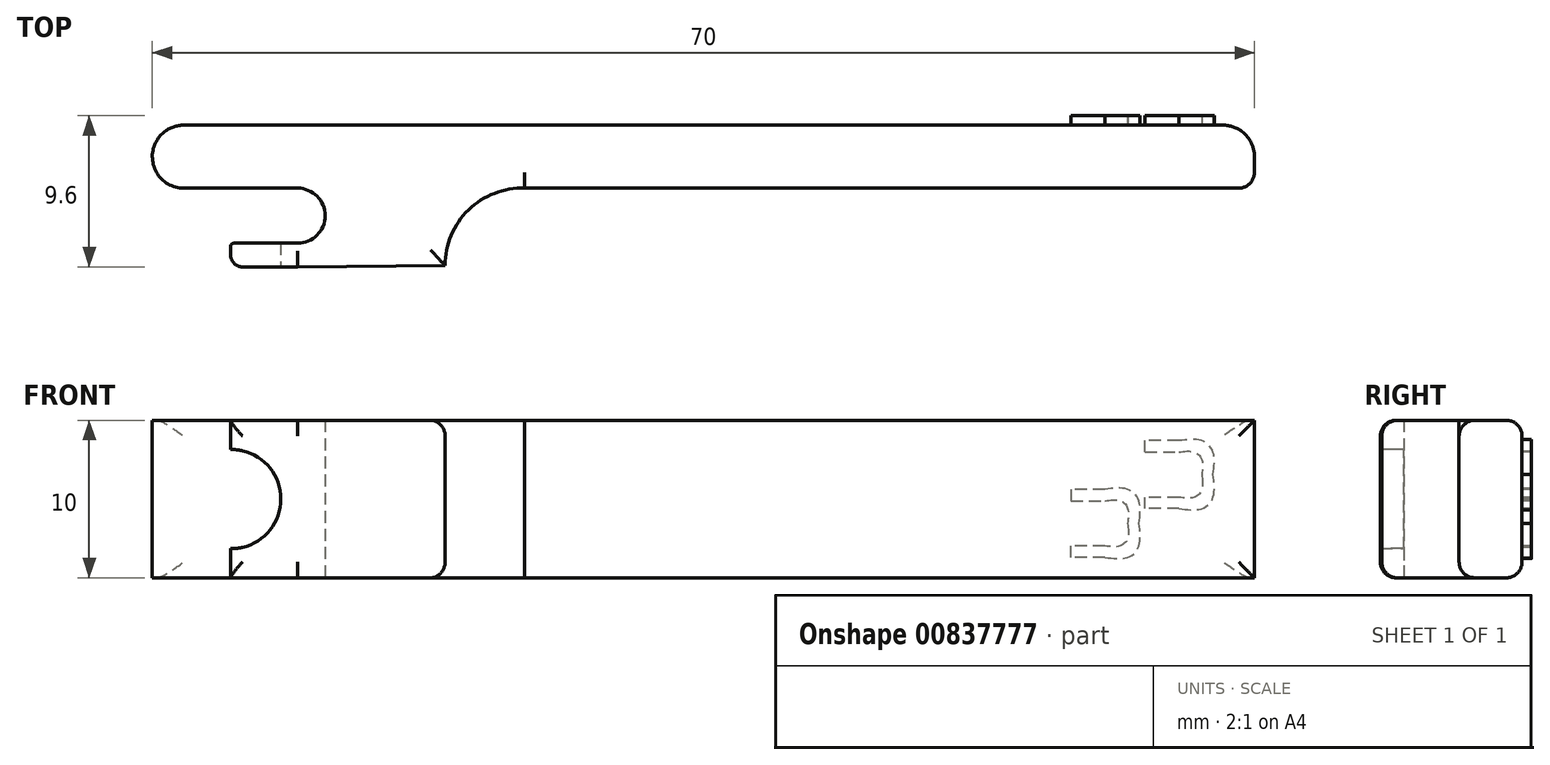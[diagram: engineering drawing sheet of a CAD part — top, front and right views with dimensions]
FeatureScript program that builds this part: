
annotation { "Feature Type Name" : "Feature", "Feature Type Description" : "" }
export const myFeature = defineFeature(function(context is Context, id is Id, definition is map)
    precondition{}
    {
        {
            var Q0;
            Q0=qCreatedBy(makeId("Top.planeOp"),FACE);
            var sketch = newSketch(context, id + "F0", { "sketchPlane" : qUnion([Q0])});
            skLineSegment(sketch, "E0.bottom", {"start": v(-27.18, 4) * mm, "end": v(38.82, 4) * mm});
            skLineSegment(sketch, "E0.top", {"start": v(-27.18, 0) * mm, "end": v(-19.95, 0) * mm});
            skLineSegment(sketch, "E0.left", {"start": v(-29.18, 2) * mm, "end": v(-29.18, 2) * mm});
            skLineSegment(sketch, "E0.right", {"start": v(40.82, 2) * mm, "end": v(40.82, 1) * mm});
            skLineSegment(sketch, "E1.bottom", {"start": v(-5.68, 0) * mm, "end": v(-4.91, 0) * mm});
            skPoint(sketch, "E2.visualSharp", {"position": v(-29.18, 0) * mm});
            skArc(sketch, "E2.filletArc", {"start": v(-29.18, 2) * mm, "mid": v(-28.6, 0.59) * mm, "end": v(-27.18, 0) * mm});
            skPoint(sketch, "E3.visualSharp", {"position": v(-29.18, 4) * mm});
            skArc(sketch, "E3.filletArc", {"start": v(-27.18, 4) * mm, "mid": v(-28.6, 3.41) * mm, "end": v(-29.18, 2) * mm});
            skArc(sketch, "E4", {"start": v(-19.95, -3.5) * mm, "mid": v(-18.2, -1.75) * mm, "end": v(-19.95, 0) * mm});
            skLineSegment(sketch, "E5.right", {"start": v(-4.91, 0) * mm, "end": v(-4.91, 0) * mm});
            skLineSegment(sketch, "E6.bottom", {"start": v(-19.95, -3.5) * mm, "end": v(-24, -3.5) * mm});
            skLineSegment(sketch, "E6.top", {"start": v(-19.95, -5) * mm, "end": v(-23.45, -5) * mm});
            skLineSegment(sketch, "E6.right", {"start": v(-24.2, -3.7) * mm, "end": v(-24.2, -4.25) * mm});
            skPoint(sketch, "E7.visualSharp", {"position": v(-24.2, -5) * mm});
            skArc(sketch, "E7.filletArc", {"start": v(-24.2, -4.25) * mm, "mid": v(-23.98, -4.78) * mm, "end": v(-23.45, -5) * mm});
            skPoint(sketch, "E8.visualSharp", {"position": v(-24.2, -3.5) * mm});
            skArc(sketch, "E8.filletArc", {"start": v(-24, -3.5) * mm, "mid": v(-24.15, -3.56) * mm, "end": v(-24.2, -3.7) * mm});
            skPoint(sketch, "E9.visualSharp", {"position": v(-4.91, -4.9) * mm});
            skPoint(sketch, "E10.visualSharp", {"position": v(40.82, 4) * mm});
            skArc(sketch, "E10.filletArc", {"start": v(40.82, 2) * mm, "mid": v(40.24, 3.41) * mm, "end": v(38.82, 4) * mm});
            skPoint(sketch, "E11.visualSharp", {"position": v(40.82, 0) * mm});
            skArc(sketch, "E11.filletArc", {"start": v(39.82, 0) * mm, "mid": v(40.53, 0.3) * mm, "end": v(40.82, 1) * mm});
            skLineSegment(sketch, "E12.trimOffspring", {"start": v(-4.91, 0) * mm, "end": v(38.32, 0) * mm});
            skLineSegment(sketch, "E13", {"start": v(-18.23, -1.41) * mm, "end": v(-18.2, -5.43) * mm, "construction": true});
            skPoint(sketch, "E13.endSnap0", {"position": v(-18.2, -1.75) * mm});
            skLineSegment(sketch, "E14.top", {"start": v(40.26, 0) * mm, "end": v(39.82, 0) * mm});
            skLineSegment(sketch, "E14.right", {"start": v(38.32, 0) * mm, "end": v(40.26, 0) * mm});
            skPoint(sketch, "E15.end.orphan", {"position": v(-10.58, -4.91) * mm});
            skArc(sketch, "E16", {"start": v(-5.52, 0) * mm, "mid": v(-9.1, -1.38) * mm, "end": v(-10.58, -4.91) * mm});
            skLineSegment(sketch, "E17", {"start": v(-19.95, -5) * mm, "end": v(-10.58, -4.91) * mm});
            skSolve(sketch);
        }
        {
            var Q0;
            Q0=makeQuery(id+"F0.imprint","IMPRINT",FACE,{"disambiguationData":[TD([[makeQuery(id+"F0.imprint","IMPRINT",EDGE,{"derivedFrom":sQuery(id+"F0.wireOp",EDGE,"E0.bottom")}),-1.0]])]});
            extrude(context, id + "F1", {"entities" : qUnion([Q0]), "depth" : 10 * mm, "offsetDistance" : 25 * mm});
        }
        {
            var Q0;
            Q0=makeQuery(id+"F1.opExtrude","CAP_EDGE",EDGE,{"disambiguationData":[OSD([sQuery(id+"F0.wireOp",EDGE,"E12.trimOffspring")])],"isStart":false});
            var Q1;
            Q1=makeQuery(id+"F1.opExtrude","CAP_EDGE",EDGE,{"disambiguationData":[OSD([sQuery(id+"F0.wireOp",EDGE,"E9.filletArc")])],"isStart":false});
            var Q2;
            Q2=makeQuery(id+"F1.opExtrude","CAP_EDGE",EDGE,{"disambiguationData":[OSD([sQuery(id+"F0.wireOp",EDGE,"E9.filletArc")])],"isStart":true});
            var Q3;
            Q3=makeQuery(id+"F1.opExtrude","CAP_EDGE",EDGE,{"disambiguationData":[OSD([sQuery(id+"F0.wireOp",EDGE,"E5.top"),sQuery(id+"F0.wireOp",EDGE,"E6.top")])],"isStart":true});
            var Q4;
            Q4=makeQuery(id+"F1.opExtrude","CAP_EDGE",EDGE,{"disambiguationData":[OSD([sQuery(id+"F0.wireOp",EDGE,"E12.trimOffspring")])],"isStart":true});
            var Q5;
            Q5=makeQuery(id+"F1.opExtrude","CAP_EDGE",EDGE,{"disambiguationData":[OSD([sQuery(id+"F0.wireOp",EDGE,"E0.bottom")])],"isStart":true});
            var Q6;
            Q6=makeQuery(id+"F1.opExtrude","CAP_EDGE",EDGE,{"disambiguationData":[OSD([sQuery(id+"F0.wireOp",EDGE,"E0.bottom")])],"isStart":false});
            var Q7;
            Q7=makeQuery(id+"F1.opExtrude","CAP_EDGE",EDGE,{"disambiguationData":[OSD([sQuery(id+"F0.wireOp",EDGE,"E5.top"),sQuery(id+"F0.wireOp",EDGE,"E6.top")])],"isStart":false});
            var Q8;
            Q8=makeQuery(id+"F1.opExtrude","SWEPT_EDGE",EDGE,{"disambiguationData":[OSD([sQuery(id+"F0.wireOp",EDGE,"E9.filletArc"),sQuery(id+"F0.wireOp",EDGE,"E15")])]});
            var Q9;
            Q9=makeQuery(id+"F1.opExtrude","SWEPT_EDGE",EDGE,{"disambiguationData":[OSD([sQuery(id+"F0.wireOp",EDGE,"E5.top"),sQuery(id+"F0.wireOp",EDGE,"E9.filletArc")])]});
            fillet(context, id + "F2", {"entities" : qUnion([Q0, Q1, Q2, Q3, Q4, Q5, Q6, Q7, Q8, Q9]), "radius" : 1 * mm, "allowEdgeOverflow" : false});
        }
        {
            var Q0;
            Q0=makeQuery(id+"F1.opExtrude","SWEPT_FACE",FACE,{"disambiguationData":[OSD([sQuery(id+"F0.wireOp",EDGE,"E0.bottom")])]});
            var sketch = newSketch(context, id + "F3", { "sketchPlane" : qUnion([Q0])});
            skLineSegment(sketch, "E18", {"start": v(-31.33, 2.02) * mm, "end": v(-29.17, 2.02) * mm});
            skLineSegment(sketch, "E19", {"start": v(-31.33, 5.62) * mm, "end": v(-29.17, 5.62) * mm});
            skLineSegment(sketch, "E20", {"start": v(-29.17, 5.62) * mm, "end": v(-29.17, 4.9) * mm});
            skLineSegment(sketch, "E21", {"start": v(-29.17, 4.9) * mm, "end": v(-31.33, 4.9) * mm});
            skFitSpline(sketch, "E22", {"points": [v(-31.33, 1.3) * mm, v(-32.77, 1.3) * mm, v(-33.49, 2.02) * mm, v(-33.49, 3.46) * mm]});
            skFitSpline(sketch, "E23", {"points": [v(-33.49, 3.46) * mm, v(-33.49, 4.9) * mm, v(-32.77, 5.62) * mm, v(-31.33, 5.62) * mm]});
            skFitSpline(sketch, "E24", {"points": [v(-31.33, 4.9) * mm, v(-32.29, 4.9) * mm, v(-32.77, 4.42) * mm, v(-32.77, 3.46) * mm]});
            skFitSpline(sketch, "E25", {"points": [v(-32.77, 3.46) * mm, v(-32.77, 2.5) * mm, v(-32.29, 2.02) * mm, v(-31.33, 2.02) * mm]});
            skLineSegment(sketch, "E26", {"start": v(-31.33, 1.3) * mm, "end": v(-29.17, 1.3) * mm});
            skLineSegment(sketch, "E27", {"start": v(-29.17, 1.3) * mm, "end": v(-29.17, 2.02) * mm});
            skLineSegment(sketch, "E28", {"start": v(-36.22, 5.11) * mm, "end": v(-33.88, 5.11) * mm});
            skLineSegment(sketch, "E29", {"start": v(-36.04, 8.7) * mm, "end": v(-33.88, 8.7) * mm});
            skLineSegment(sketch, "E30", {"start": v(-33.88, 7.99) * mm, "end": v(-36.04, 7.99) * mm});
            skFitSpline(sketch, "E31", {"points": [v(-36.04, 4.4) * mm, v(-37.47, 4.4) * mm, v(-38.2, 5.11) * mm, v(-38.2, 6.55) * mm]});
            skFitSpline(sketch, "E32", {"points": [v(-38.2, 6.55) * mm, v(-38.2, 7.99) * mm, v(-37.47, 8.7) * mm, v(-36.04, 8.7) * mm]});
            skFitSpline(sketch, "E33", {"points": [v(-36.04, 7.99) * mm, v(-37, 7.99) * mm, v(-37.47, 7.5) * mm, v(-37.47, 6.55) * mm]});
            skFitSpline(sketch, "E34", {"points": [v(-37.47, 6.55) * mm, v(-37.47, 5.6) * mm, v(-37, 5.11) * mm, v(-36.04, 5.11) * mm]});
            skLineSegment(sketch, "E35", {"start": v(-36.04, 4.4) * mm, "end": v(-33.88, 4.4) * mm});
            skLineSegment(sketch, "E36", {"start": v(-33.88, 4.4) * mm, "end": v(-33.88, 5.11) * mm});
            skLineSegment(sketch, "E37", {"start": v(-33.88, 7.99) * mm, "end": v(-33.88, 8.7) * mm});
            skSolve(sketch);
        }
        {
            var Q0;
            Q0=makeQuery(id+"F3.imprint","IMPRINT",FACE,{"disambiguationData":[TD([[makeQuery(id+"F3.imprint","IMPRINT",EDGE,{"derivedFrom":sQuery(id+"F3.wireOp",EDGE,"E18")}),-1.0]])]});
            var Q1;
            Q1=makeQuery(id+"F3.imprint","IMPRINT",FACE,{"disambiguationData":[TD([[makeQuery(id+"F3.imprint","IMPRINT",EDGE,{"derivedFrom":sQuery(id+"F3.wireOp",EDGE,"E29")}),-1.0]])]});
            extrude(context, id + "F4", {"entities" : qUnion([Q0, Q1]), "operationType" : NewBodyOperationType.ADD, "depth" : 0.6 * mm, "offsetDistance" : 25 * mm});
        }
        {
            var Q0;
            Q0=makeQuery(id+"F1.opExtrude","SWEPT_FACE",FACE,{"disambiguationData":[OSD([sQuery(id+"F0.wireOp",EDGE,"E5.top"),sQuery(id+"F0.wireOp",EDGE,"E6.top")])]});
            var sketch = newSketch(context, id + "F5", { "sketchPlane" : qUnion([Q0])});
            skLineSegment(sketch, "E38", {"start": v(-23.45, 5) * mm, "end": v(-17.62, 5) * mm, "construction": true});
            skCircle(sketch, "E39", {"center": v(-24.17, 5) * mm, "radius": 3.15 * mm});
            skSolve(sketch);
        }
        {
            var Q0;
            {var subQ0=sQuery(id+"F5.wireOp",EDGE,"E39");var subQ1=makeQuery(id+"F1.opExtrude","SWEPT_EDGE",EDGE,{"disambiguationData":[OSD([sQuery(id+"F0.wireOp",EDGE,"E6.top"),sQuery(id+"F0.wireOp",EDGE,"E7.filletArc")])]});var subQ2=makeQuery(id+"F5.imprint","INTERSECT",VERTEX,{"disambiguationData":[OD(0.0)],"derivedFrom":[subQ1,subQ0]});Q0=makeQuery(id+"F5.imprint","IMPRINT",FACE,{"disambiguationData":[TD([[makeQuery(id+"F5.imprint","IMPRINT",EDGE,{"disambiguationData":[TD([[subQ2,1.0]])],"derivedFrom":subQ0}),1.0]])]});}
            var Q1;
            {var subQ0=sQuery(id+"F5.wireOp",EDGE,"E39");var subQ1=makeQuery(id+"F1.opExtrude","SWEPT_EDGE",EDGE,{"disambiguationData":[OSD([sQuery(id+"F0.wireOp",EDGE,"E6.top"),sQuery(id+"F0.wireOp",EDGE,"E7.filletArc")])]});var subQ2=makeQuery(id+"F5.imprint","INTERSECT",VERTEX,{"disambiguationData":[OD(0.0)],"derivedFrom":[subQ1,subQ0]});Q1=makeQuery(id+"F5.imprint","IMPRINT",FACE,{"disambiguationData":[TD([[makeQuery(id+"F5.imprint","IMPRINT",EDGE,{"disambiguationData":[TD([[subQ2,-1.0]])],"derivedFrom":subQ0}),1.0]])]});}
            extrude(context, id + "F6", {"entities" : qUnion([Q0, Q1]), "operationType" : NewBodyOperationType.REMOVE, "oppositeDirection" : true, "depth" : 2 * mm, "offsetDistance" : 25 * mm});
        }
    });
